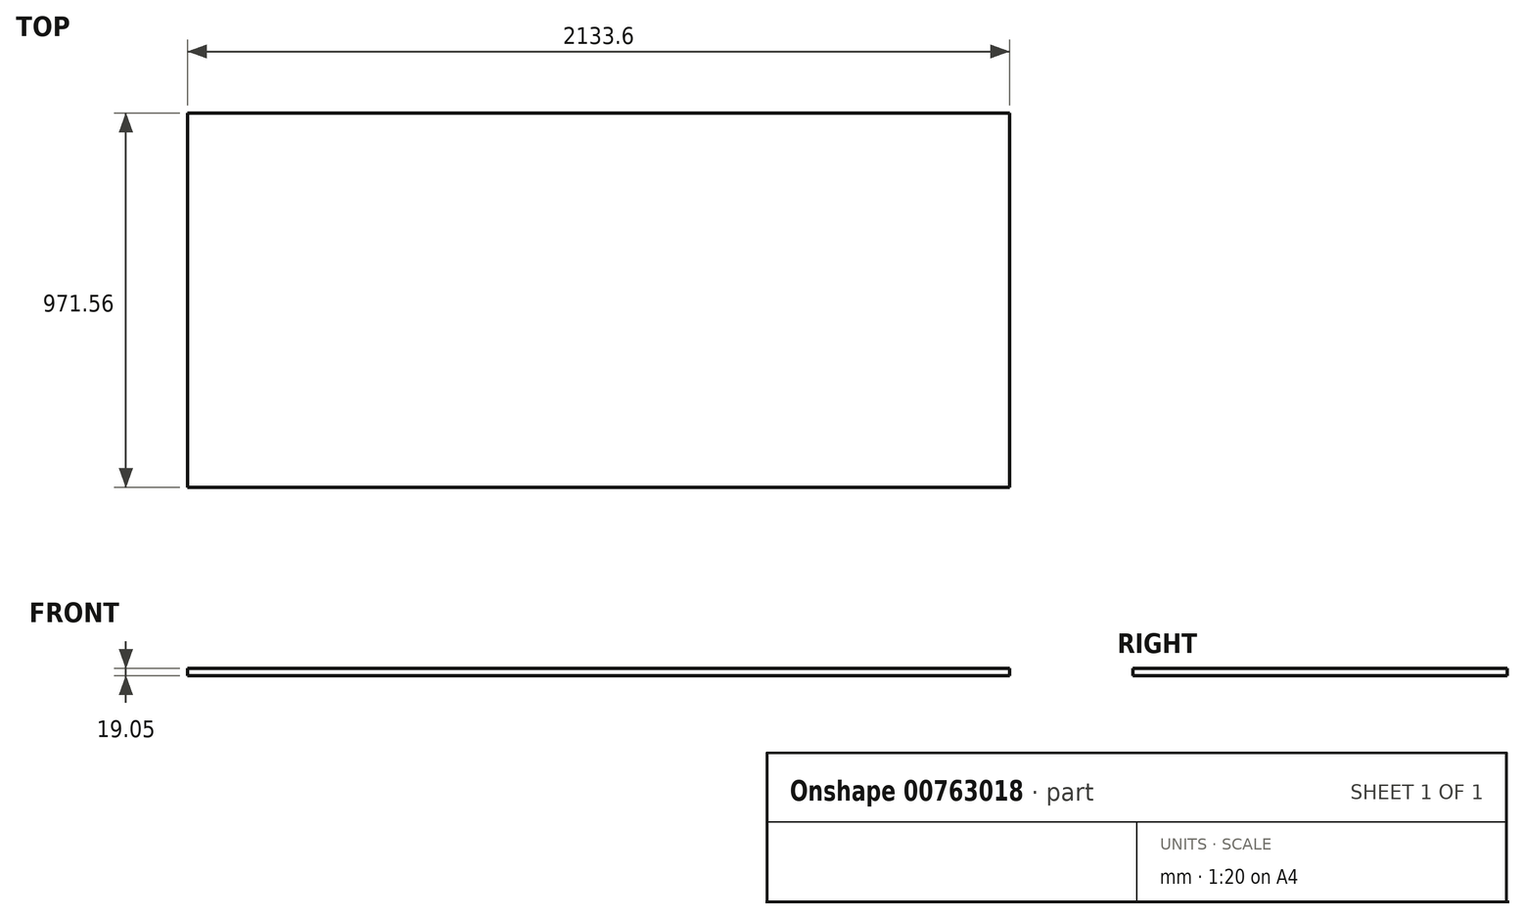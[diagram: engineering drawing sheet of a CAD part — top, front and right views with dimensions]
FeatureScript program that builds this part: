
annotation { "Feature Type Name" : "Feature", "Feature Type Description" : "" }
export const myFeature = defineFeature(function(context is Context, id is Id, definition is map)
    precondition{}
    {
        {
            var Q0;
            Q0=qCreatedBy(makeId("Top.planeOp"),FACE);
            var sketch = newSketch(context, id + "F0", { "sketchPlane" : qUnion([Q0])});
            skLineSegment(sketch, "E0.bottom", {"start": v(1066.8, 485.78) * mm, "end": v(-1066.8, 485.78) * mm});
            skLineSegment(sketch, "E0.top", {"start": v(1066.8, -485.78) * mm, "end": v(-1066.8, -485.78) * mm});
            skLineSegment(sketch, "E0.left", {"start": v(1066.8, 485.78) * mm, "end": v(1066.8, -485.78) * mm});
            skLineSegment(sketch, "E0.right", {"start": v(-1066.8, 485.78) * mm, "end": v(-1066.8, -485.78) * mm});
            skPoint(sketch, "E0.middle", {"position": v(0, 0) * mm});
            skSolve(sketch);
        }
        {
            var Q0;
            Q0=makeQuery(id+"F0.imprint","IMPRINT",FACE,{"disambiguationData":[TD([[makeQuery(id+"F0.imprint","IMPRINT",EDGE,{"derivedFrom":sQuery(id+"F0.wireOp",EDGE,"E0.bottom")}),1.0]])]});
            extrude(context, id + "F1", {"entities" : qUnion([Q0]), "depth" : 19.05 * mm, "offsetDistance" : 25.4 * mm});
        }
    });
